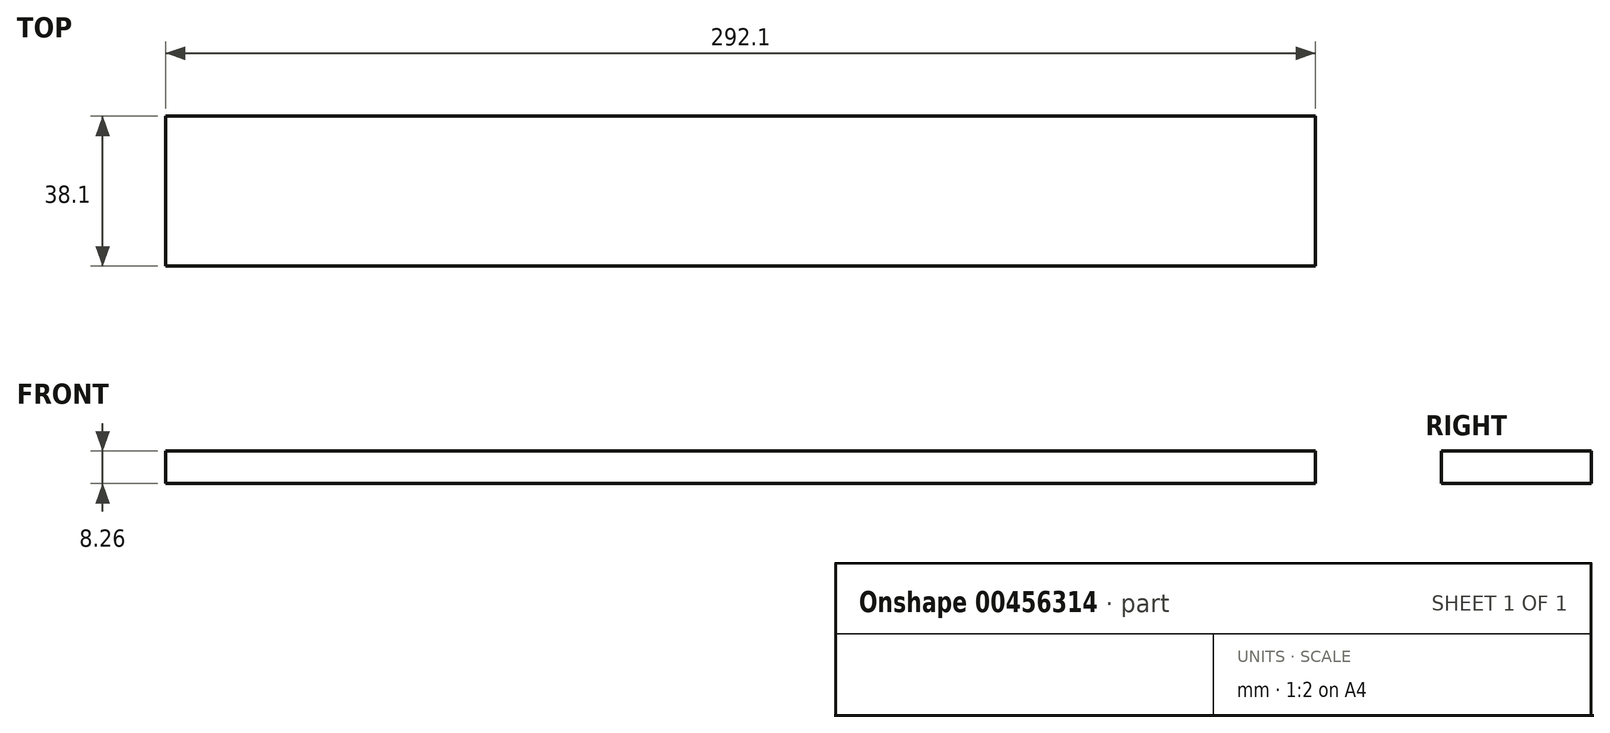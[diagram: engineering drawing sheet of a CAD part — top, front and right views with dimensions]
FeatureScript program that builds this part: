
annotation { "Feature Type Name" : "Feature", "Feature Type Description" : "" }
export const myFeature = defineFeature(function(context is Context, id is Id, definition is map)
    precondition{}
    {
        {
            var Q0;
            Q0=qCreatedBy(makeId("Top.planeOp"),FACE);
            var sketch = newSketch(context, id + "F0", { "sketchPlane" : qUnion([Q0])});
            skLineSegment(sketch, "E0.bottom", {"start": v(0, 0) * mm, "end": v(292.1, 0) * mm});
            skLineSegment(sketch, "E0.top", {"start": v(0, 38.1) * mm, "end": v(292.1, 38.1) * mm});
            skLineSegment(sketch, "E0.left", {"start": v(0, 0) * mm, "end": v(0, 38.1) * mm});
            skLineSegment(sketch, "E0.right", {"start": v(292.1, 0) * mm, "end": v(292.1, 38.1) * mm});
            skSolve(sketch);
        }
        {
            var Q0;
            Q0=makeQuery(id+"F0.imprint","IMPRINT",FACE,{"disambiguationData":[TD([[makeQuery(id+"F0.imprint","IMPRINT",EDGE,{"derivedFrom":sQuery(id+"F0.wireOp",EDGE,"E0.bottom")}),1.0]])]});
            extrude(context, id + "F1", {"entities" : qUnion([Q0]), "depth" : 8.25 * mm});
        }
    });
